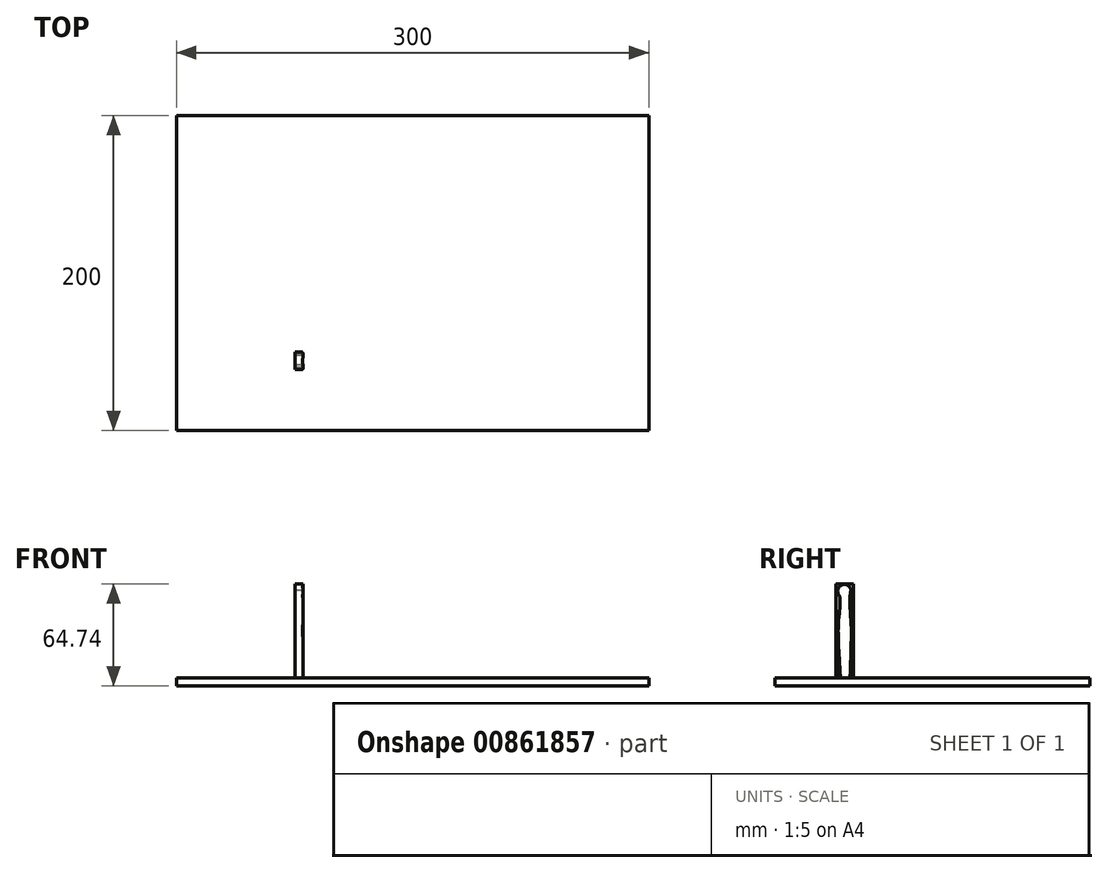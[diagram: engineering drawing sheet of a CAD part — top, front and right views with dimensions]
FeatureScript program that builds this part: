
annotation { "Feature Type Name" : "Feature", "Feature Type Description" : "" }
export const myFeature = defineFeature(function(context is Context, id is Id, definition is map)
    precondition{}
    {
        {
            var Q0;
            Q0=qCreatedBy(makeId("Top.planeOp"),FACE);
            var sketch = newSketch(context, id + "F0", { "sketchPlane" : qUnion([Q0])});
            skLineSegment(sketch, "E0.bottom", {"start": v(150, -100) * mm, "end": v(-150, -100) * mm});
            skLineSegment(sketch, "E0.top", {"start": v(150, 100) * mm, "end": v(-150, 100) * mm});
            skLineSegment(sketch, "E0.left", {"start": v(150, -100) * mm, "end": v(150, 100) * mm});
            skLineSegment(sketch, "E0.right", {"start": v(-150, -100) * mm, "end": v(-150, 100) * mm});
            skPoint(sketch, "E0.middle", {"position": v(0, 0) * mm});
            skSolve(sketch);
        }
        {
            var Q0;
            Q0=makeQuery(id+"F0.imprint","IMPRINT",FACE,{"disambiguationData":[TD([[makeQuery(id+"F0.imprint","IMPRINT",EDGE,{"derivedFrom":sQuery(id+"F0.wireOp",EDGE,"E0.bottom")}),-1.0]])]});
            extrude(context, id + "F1", {"entities" : qUnion([Q0]), "depth" : 5 * mm, "offsetDistance" : 25 * mm});
        }
        {
            var Q0;
            Q0=qCreatedBy(makeId("Front.planeOp"),FACE);
            var sketch = newSketch(context, id + "F2", { "sketchPlane" : qUnion([Q0])});
            skLineSegment(sketch, "E1.bottom", {"start": v(-74.74, 4.74) * mm, "end": v(-69.74, 4.74) * mm});
            skLineSegment(sketch, "E1.top", {"start": v(-74.74, 64.74) * mm, "end": v(-69.74, 64.74) * mm});
            skLineSegment(sketch, "E1.left", {"start": v(-74.74, 4.74) * mm, "end": v(-74.74, 64.74) * mm});
            skLineSegment(sketch, "E1.right", {"start": v(-69.74, 4.74) * mm, "end": v(-69.74, 64.74) * mm});
            skSolve(sketch);
        }
        {
            var Q0;
            Q0=makeQuery(id+"F2.imprint","IMPRINT",FACE,{"disambiguationData":[TD([[makeQuery(id+"F2.imprint","IMPRINT",EDGE,{"derivedFrom":sQuery(id+"F2.wireOp",EDGE,"E1.bottom")}),1.0]])]});
            extrude(context, id + "F3", {"entities" : qUnion([Q0]), "operationType" : NewBodyOperationType.ADD, "depth" : 100 * mm, "offsetDistance" : 25 * mm});
        }
        {
            var Q0;
            Q0=makeQuery(id+"F3.opExtrude","SWEPT_FACE",FACE,{"disambiguationData":[OSD([sQuery(id+"F2.wireOp",EDGE,"E1.left")])]});
            var sketch = newSketch(context, id + "F4", { "sketchPlane" : qUnion([Q0])});
            skLineSegment(sketch, "E2.bottom", {"start": v(0, 64.74) * mm, "end": v(50, 64.74) * mm});
            skLineSegment(sketch, "E2.top", {"start": v(0, 5) * mm, "end": v(50, 5) * mm});
            skLineSegment(sketch, "E2.left", {"start": v(0, 64.74) * mm, "end": v(0, 5) * mm});
            skLineSegment(sketch, "E2.right", {"start": v(50, 64.74) * mm, "end": v(50, 5) * mm});
            skLineSegment(sketch, "E3.bottom", {"start": v(61.12, 5) * mm, "end": v(100, 5) * mm});
            skLineSegment(sketch, "E3.top", {"start": v(61.12, 64.74) * mm, "end": v(100, 64.74) * mm});
            skLineSegment(sketch, "E3.left", {"start": v(61.12, 5) * mm, "end": v(61.12, 64.74) * mm});
            skLineSegment(sketch, "E3.right", {"start": v(100, 5) * mm, "end": v(100, 64.74) * mm});
            skSolve(sketch);
        }
        {
            var Q0;
            Q0=makeQuery(id+"F4.imprint","IMPRINT",FACE,{"disambiguationData":[TD([[makeQuery(id+"F4.imprint","IMPRINT",EDGE,{"derivedFrom":sQuery(id+"F4.wireOp",EDGE,"E2.bottom")}),1.0]])]});
            var Q1;
            Q1=makeQuery(id+"F4.imprint","IMPRINT",FACE,{"disambiguationData":[TD([[makeQuery(id+"F4.imprint","IMPRINT",EDGE,{"derivedFrom":sQuery(id+"F4.wireOp",EDGE,"E3.bottom")}),1.0]])]});
            extrude(context, id + "F5", {"entities" : qUnion([Q0, Q1]), "operationType" : NewBodyOperationType.REMOVE, "oppositeDirection" : true, "depth" : 25 * mm, "offsetDistance" : 25 * mm});
        }
        {
            var Q0;
            Q0=makeQuery(id+"F3.opExtrude","SWEPT_FACE",FACE,{"disambiguationData":[OSD([sQuery(id+"F2.wireOp",EDGE,"E1.left")])]});
            var sketch = newSketch(context, id + "F6", { "sketchPlane" : qUnion([Q0])});
            skFitSpline(sketch, "E4", {"points": [v(52.24, 5) * mm, v(52.9, 47.23) * mm, v(54.48, 46.83) * mm], "startDerivative": vector(-2.9, 72.65) * mm, "endDerivative": vector(10.37, -6.76) * mm});
            skFitSpline(sketch, "E5", {"points": [v(58.31, 5) * mm, v(58.44, 47.62) * mm, v(55.8, 50.13) * mm], "startDerivative": vector(4.75, 72.1) * mm, "endDerivative": vector(-13, 6.11) * mm});
            skFitSpline(sketch, "E6", {"points": [v(51.94, 44.52) * mm, v(51.45, 61.08) * mm, v(50, 62.4) * mm], "startDerivative": vector(1.22, 28.62) * mm, "endDerivative": vector(-6.3, 2.97) * mm});
            skFitSpline(sketch, "E7", {"points": [v(58.95, 46.01) * mm, v(59.9, 62.27) * mm, v(63.2, 60.3) * mm, v(63.06, 40.5) * mm], "startDerivative": vector(-3.75, 58.34) * mm, "endDerivative": vector(-7.55, -56.2) * mm});
            skCircle(sketch, "E8", {"center": v(55.8, 60.16) * mm, "radius": 4.26 * mm});
            skSolve(sketch);
        }
        {
            var Q0;
            {var subQ0=sQuery(id+"F6.wireOp",EDGE,"E8");var subQ1=sQuery(id+"F6.wireOp",EDGE,"E6");var subQ2=makeQuery(id+"F6.imprint","INTERSECT",VERTEX,{"disambiguationData":[OD(0.0)],"derivedFrom":[subQ1,subQ0]});Q0=makeQuery(id+"F6.imprint","IMPRINT",FACE,{"disambiguationData":[TD([[makeQuery(id+"F6.imprint","IMPRINT",EDGE,{"disambiguationData":[TD([[subQ2,-1.0]])],"derivedFrom":subQ1}),-1.0]])]});}
            var Q1;
            {var subQ0=sQuery(id+"F6.wireOp",EDGE,"E8");var subQ1=sQuery(id+"F6.wireOp",EDGE,"E7");var subQ2=makeQuery(id+"F6.imprint","INTERSECT",VERTEX,{"disambiguationData":[OD(0.0)],"derivedFrom":[subQ1,subQ0]});Q1=makeQuery(id+"F6.imprint","IMPRINT",FACE,{"disambiguationData":[TD([[makeQuery(id+"F6.imprint","IMPRINT",EDGE,{"disambiguationData":[TD([[subQ2,-1.0]])],"derivedFrom":subQ1}),-1.0]])]});}
            var Q2;
            {var subQ0=sQuery(id+"F6.wireOp",EDGE,"E6");var subQ1=sQuery(id+"F6.wireOp",EDGE,"E4");var subQ2=makeQuery(id+"F6.imprint","INTERSECT",VERTEX,{"derivedFrom":[subQ1,subQ0]});Q2=makeQuery(id+"F6.imprint","IMPRINT",FACE,{"disambiguationData":[TD([[makeQuery(id+"F6.imprint","IMPRINT",EDGE,{"disambiguationData":[TD([[subQ2,-1.0]])],"derivedFrom":subQ0}),-1.0]])]});}
            extrude(context, id + "F7", {"entities" : qUnion([Q0, Q1, Q2]), "operationType" : NewBodyOperationType.REMOVE, "oppositeDirection" : true, "depth" : 25 * mm, "offsetDistance" : 25 * mm});
        }
        {
            var Q0;
            Q0=makeQuery(id+"F7.boolean.opBoolean","COPY",EDGE,{"derivedFrom":makeQuery(id+"F7.opExtrude","SWEPT_EDGE",EDGE,{"disambiguationData":[OSD([sQuery(id+"F6.wireOp",EDGE,"E7"),sQuery(id+"F6.wireOp",EDGE,"E8")])]})});
            var Q1;
            Q1=makeQuery(id+"F7.boolean.opBoolean","COPY",EDGE,{"derivedFrom":makeQuery(id+"F7.opExtrude","SWEPT_EDGE",EDGE,{"disambiguationData":[OSD([sQuery(id+"F6.wireOp",EDGE,"E5"),sQuery(id+"F6.wireOp",EDGE,"E7")])]})});
            var Q2;
            Q2=makeQuery(id+"F7.boolean.opBoolean","COPY",EDGE,{"derivedFrom":makeQuery(id+"F7.opExtrude","SWEPT_EDGE",EDGE,{"disambiguationData":[OSD([sQuery(id+"F6.wireOp",EDGE,"E4"),sQuery(id+"F6.wireOp",EDGE,"E6")])]})});
            fillet(context, id + "F8", {"entities" : qUnion([Q0, Q1, Q2]), "radius" : 5 * mm, "tangentPropagation" : true, "allowEdgeOverflow" : false});
        }
        {
            var Q0;
            Q0=makeQuery(id+"F7.boolean.opBoolean","COPY",EDGE,{"derivedFrom":makeQuery(id+"F7.opExtrude","CAP_EDGE",EDGE,{"disambiguationData":[OSD([sQuery(id+"F6.wireOp",EDGE,"E8")])],"isStart":true})});
            var Q1;
            Q1=makeQuery(id+"F7.boolean.opBoolean","COPY",EDGE,{"derivedFrom":makeQuery(id+"F7.opExtrude","CAP_EDGE",EDGE,{"disambiguationData":[OSD([sQuery(id+"F6.wireOp",EDGE,"E6")])],"isStart":true})});
            var Q2;
            Q2=makeQuery(id+"F7.boolean.opBoolean","INTERSECT",EDGE,{"derivedFrom":[makeQuery(id+"F3.opExtrude","SWEPT_FACE",FACE,{"disambiguationData":[OSD([sQuery(id+"F2.wireOp",EDGE,"E1.right")])]}),makeQuery(id+"F7.opExtrude","SWEPT_FACE",FACE,{"disambiguationData":[OSD([sQuery(id+"F6.wireOp",EDGE,"E6")])]})]});
            var Q3;
            Q3=makeQuery(id+"F7.boolean.opBoolean","INTERSECT",EDGE,{"derivedFrom":[makeQuery(id+"F3.opExtrude","SWEPT_FACE",FACE,{"disambiguationData":[OSD([sQuery(id+"F2.wireOp",EDGE,"E1.right")])]}),makeQuery(id+"F7.opExtrude","SWEPT_FACE",FACE,{"disambiguationData":[OSD([sQuery(id+"F6.wireOp",EDGE,"E8")])]})]});
            fillet(context, id + "F9", {"entities" : qUnion([Q0, Q1, Q2, Q3]), "radius" : 1 * mm, "tangentPropagation" : true, "allowEdgeOverflow" : false});
        }
        {
            var Q0;
            Q0=makeQuery(id+"F5.boolean.opBoolean","INTERSECT",EDGE,{"derivedFrom":[makeQuery(id+"F3.opExtrude","SWEPT_FACE",FACE,{"disambiguationData":[OSD([sQuery(id+"F2.wireOp",EDGE,"E1.right")])]}),makeQuery(id+"F5.opExtrude","SWEPT_FACE",FACE,{"disambiguationData":[OSD([sQuery(id+"F4.wireOp",EDGE,"E3.left")])]})]});
            var Q1;
            Q1=makeQuery(id+"F5.boolean.opBoolean","INTERSECT",EDGE,{"derivedFrom":[makeQuery(id+"F3.opExtrude","SWEPT_FACE",FACE,{"disambiguationData":[OSD([sQuery(id+"F2.wireOp",EDGE,"E1.right")])]}),makeQuery(id+"F5.opExtrude","SWEPT_FACE",FACE,{"disambiguationData":[OSD([sQuery(id+"F4.wireOp",EDGE,"E2.right")])]})]});
            var Q2;
            Q2=makeQuery(id+"F5.boolean.opBoolean","COPY",EDGE,{"derivedFrom":makeQuery(id+"F5.opExtrude","CAP_EDGE",EDGE,{"disambiguationData":[OSD([sQuery(id+"F4.wireOp",EDGE,"E3.left")])],"isStart":true})});
            var Q3;
            Q3=makeQuery(id+"F5.boolean.opBoolean","COPY",EDGE,{"derivedFrom":makeQuery(id+"F5.opExtrude","CAP_EDGE",EDGE,{"disambiguationData":[OSD([sQuery(id+"F4.wireOp",EDGE,"E2.right")])],"isStart":true})});
            fillet(context, id + "F10", {"entities" : qUnion([Q0, Q1, Q2, Q3]), "radius" : 1 * mm, "tangentPropagation" : true, "allowEdgeOverflow" : false});
        }
    });
